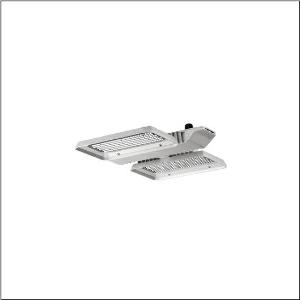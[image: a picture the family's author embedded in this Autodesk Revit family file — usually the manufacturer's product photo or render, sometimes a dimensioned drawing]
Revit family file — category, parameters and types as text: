
# Revit family: highbay_11_51hl61d14dca
name_source: partatom
category: Lighting Fixtures
units: mm (PartAtom-declared; Revit-internal decimal feet)

## family parameters
Cut with Voids When Loaded = No
Host = Face
Light Source = No
Part Type = Normal
Room Calculation Point = No
Round Connector Dimension = Use Diameter
Shared = No

## types (1)
- --- (1 x LED, 9790 lm, 55.6 W, 4000K)
    Apparent Load = 56 VA
    CIE Flux Codes = 88 95 99 100 99
    Color Rendering = 80
    Color Temperature = 4000K
    Default Elevation = 1800 mm
    Description = Highbay 11, LED high bay luminaire, primary light control with lens, of PMMA, light emission: direct distribution, primary light characteristic: symmetric, installation type: surface-mounted, suspended mounting, for 1x 2x LED, rated luminous flux: 9.790lm, luminous efficacy: 176lm/W, light colour: 840, colour temperature: 4000K, control gear: ECG DALI, with terminal, 5-pole, max. 2.5mm², mains connection: 230..240V, AC, 50/60Hz, rated input power: 56W, LED unit, of diecast aluminium, coated, metallic grey (RAL 9006), length: 470mm, width: 500mm, height: 65mm, housing, of diecast aluminium, coated, metallic grey (RAL 9006), protection rating (complete): IP65, insulation class (complete): insulation class I (protective earthing), certification: CE, ENEC, VDE, UKCA, protection symbol: D, impact resistance: IK08 with glass or PC cover, permissible operating ambient temperature: -35..+70°C, corresponds to IFS (International Featured Standards) requirements for safety and quality in the food industry, reducing of maximum allowable ambient temperature of 5°C with ceiling mounting, packaging unit: 1 piece
    Height = 95 mm
    Lamp = 1 x LED
    Lamp Light Flux = 9790 lm
    Lamp Power = 55.6 W
    Lamp count = 1
    Length = 468 mm
    Luminous efficacy = 176 lm/W
    Manufacturer = Siteco
    ModVariant = No
    Model = 51HL61D14DCA
    Mounting Place = Ceiling
    Mounting Type = Pendant
    Number of Poles = 1
    OnlyDefault = Yes
    Power Factor = 1
    Product Name = Highbay 11
    Product group = LED high bay luminaire
    ProductGroupID = 903
    Protection Class = Protection class I
    Protection Degree = IP 65
    RLX_Detail_Level = 1
    RLX_Emergency_Light_Flux = 0 lm
    RLX_Emergency_Type = 0
    RLX_Emergency_Type_DB = No
    RlxData = <blob elided: 70789 chars, md5=6d539731>
    Socket = socket
    Standby Power = 0 W
    System Light Flux = 9790 lm
    System Power = 56 W
    Type Comments = factory setting: luminous flux: 100 % | dim-lin: 254 | 315 mA
    Type Image = l_1003425.jpg
    URL = http://relux.com
    VarID = @adj_160179
    Voltage = 0 V
    Weight = 0.00 kg
    Width = 501 mm

## geometry (parser evidence)
native form markers: Blend x4, Sweep x12
no freeform markers — native parametric forms only
